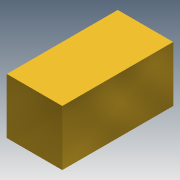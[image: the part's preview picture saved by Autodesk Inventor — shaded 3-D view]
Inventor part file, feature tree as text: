
AUTODESK INVENTOR PART (.ipt)
format: ipt  version: 2013 SP2 (Build 170200200, 200)  size: 76,288 bytes
history: native  units: in
note: dims shown in document units (in); Inventor stores cm internally (conversion verified against a paired STEP export)
features: extrude x1, sketch x1
ambient origin geometry x8: Origin, YZ Plane, XZ Plane, XY Plane, X Axis, Y Axis, Z Axis, Center Point
bodies: Solid1 (feature_tree)
feature tree (2):
  extrude  "Extrusion1"  Depth=6.0in
  sketch  "Sketch1"  dims[d0=6.0in d1=6.0in d2=12.0in d3=0.0in]
